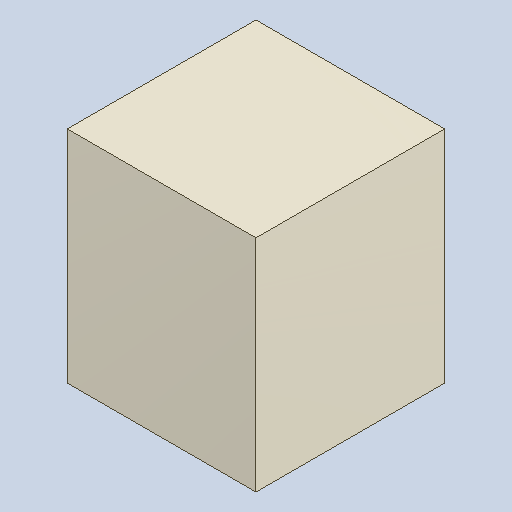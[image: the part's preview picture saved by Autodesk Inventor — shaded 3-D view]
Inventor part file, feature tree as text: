
AUTODESK INVENTOR PART (.ipt)
format: ipt  version: 2023.4 (Build 274418000, 418)  size: 82,944 bytes
history: native  units: mm
features: extrude x1
ambient origin geometry x8: Origin, YZ Plane, XZ Plane, XY Plane, X Axis, Y Axis, Z Axis, Center Point
bodies: Solid1 (feature_tree)
feature tree (1):
  extrude  "Extruded_25"  [1 undecoded]
note: 1 required parameter value undecoded (feature->parameter linkage not recoverable at this tier; creation-order binding heuristic only, values carry confidence <= 0.55)
